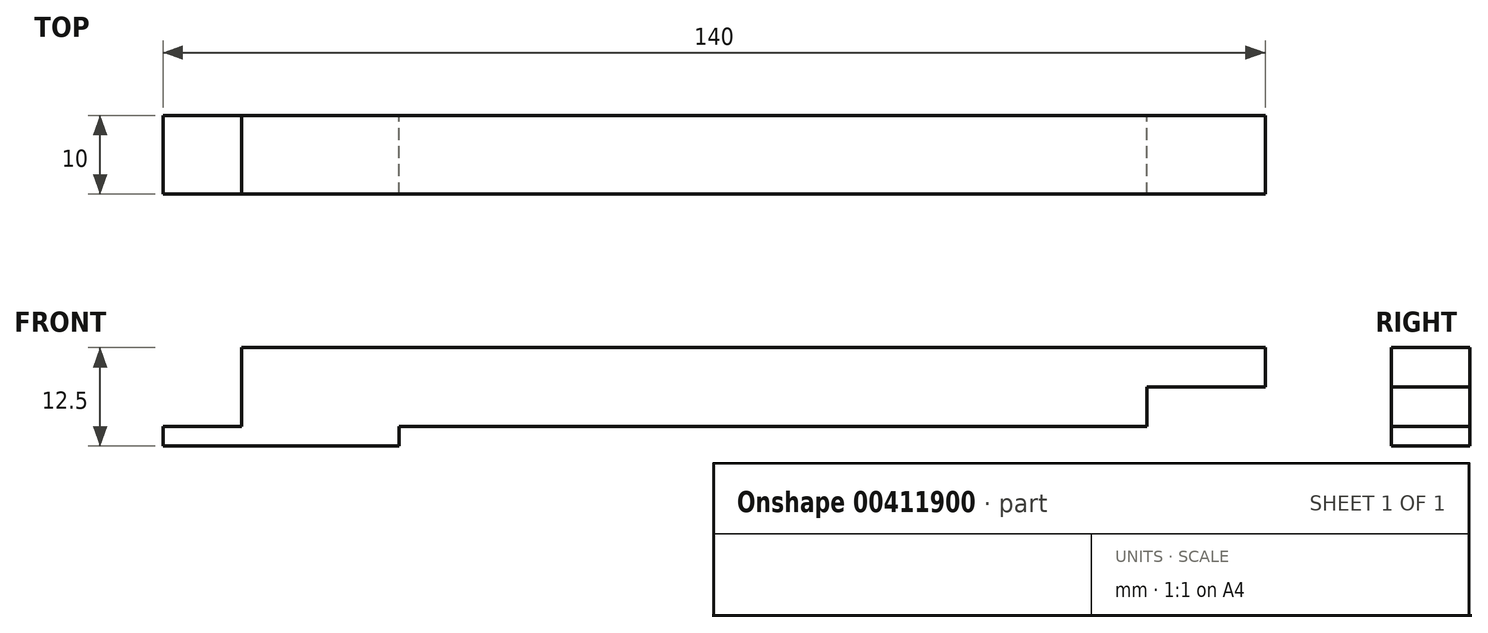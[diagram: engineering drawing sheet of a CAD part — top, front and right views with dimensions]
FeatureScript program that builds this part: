
annotation { "Feature Type Name" : "Feature", "Feature Type Description" : "" }
export const myFeature = defineFeature(function(context is Context, id is Id, definition is map)
    precondition{}
    {
        {
            var Q0;
            Q0=qCreatedBy(makeId("Front.planeOp"),FACE);
            var sketch = newSketch(context, id + "F0", { "sketchPlane" : qUnion([Q0])});
            skLineSegment(sketch, "E0.bottom", {"start": v(-57.5, 0) * mm, "end": v(57.5, 0) * mm});
            skLineSegment(sketch, "E0.top", {"start": v(-57.5, -10) * mm, "end": v(57.5, -10) * mm});
            skLineSegment(sketch, "E0.left", {"start": v(-57.5, 0) * mm, "end": v(-57.5, -10) * mm});
            skLineSegment(sketch, "E0.right", {"start": v(57.5, 0) * mm, "end": v(57.5, -10) * mm});
            skSolve(sketch);
        }
        {
            var Q0;
            Q0 = qSketchRegion(id + "F0", true);
            extrude(context, id + "F1", {"entities" : qUnion([Q0]), "depth" : 10 * mm});
        }
        {
            var Q0;
            Q0=makeQuery(id+"F1.opExtrude","SWEPT_FACE",FACE,{"disambiguationData":[OSD([sQuery(id+"F0.wireOp",EDGE,"E0.top")])]});
            var sketch = newSketch(context, id + "F2", { "sketchPlane" : qUnion([Q0])});
            skLineSegment(sketch, "E1.bottom", {"start": v(57.5, 10) * mm, "end": v(42.5, 10) * mm});
            skLineSegment(sketch, "E1.top", {"start": v(57.5, 0) * mm, "end": v(42.5, 0) * mm});
            skLineSegment(sketch, "E1.left", {"start": v(57.5, 10) * mm, "end": v(57.5, 0) * mm});
            skLineSegment(sketch, "E1.right", {"start": v(42.5, 10) * mm, "end": v(42.5, 0) * mm});
            skSolve(sketch);
        }
        {
            var Q0;
            Q0=makeQuery(id+"F2.imprint","IMPRINT",FACE,{"disambiguationData":[TD([[makeQuery(id+"F2.imprint","IMPRINT",EDGE,{"derivedFrom":sQuery(id+"F2.wireOp",EDGE,"E1.bottom")}),-1.0]])]});
            extrude(context, id + "F3", {"entities" : qUnion([Q0]), "operationType" : NewBodyOperationType.REMOVE, "oppositeDirection" : true, "depth" : 5 * mm});
        }
        {
            var Q0;
            Q0=makeQuery(id+"F1.opExtrude","SWEPT_FACE",FACE,{"disambiguationData":[OSD([sQuery(id+"F0.wireOp",EDGE,"E0.top")])]});
            var sketch = newSketch(context, id + "F4", { "sketchPlane" : qUnion([Q0])});
            skLineSegment(sketch, "E2.bottom", {"start": v(-52.5, 10) * mm, "end": v(-77.5, 10) * mm});
            skLineSegment(sketch, "E2.top", {"start": v(-52.5, 0) * mm, "end": v(-77.5, 0) * mm});
            skLineSegment(sketch, "E2.left", {"start": v(-52.5, 10) * mm, "end": v(-52.5, 0) * mm});
            skLineSegment(sketch, "E2.right", {"start": v(-77.5, 10) * mm, "end": v(-77.5, 0) * mm});
            skSolve(sketch);
        }
        {
            var Q0;
            {var subQ3=sQuery(id+"F4.wireOp",EDGE,"E2.left");Q0=makeQuery(id+"F4.imprint","IMPRINT",FACE,{"disambiguationData":[TD([[makeQuery(id+"F4.imprint","IMPRINT",EDGE,{"derivedFrom":subQ3}),-1.0]])]});}
            var Q1;
            {var subQ2=sQuery(id+"F4.wireOp",EDGE,"E2.right");Q1=makeQuery(id+"F4.imprint","IMPRINT",FACE,{"disambiguationData":[TD([[makeQuery(id+"F4.imprint","IMPRINT",EDGE,{"derivedFrom":subQ2}),1.0]])]});}
            extrude(context, id + "F5", {"entities" : qUnion([Q0, Q1]), "operationType" : NewBodyOperationType.ADD, "depth" : 2.5 * mm});
        }
        {
            var Q0;
            Q0=makeQuery(id+"F1.opExtrude","SWEPT_FACE",FACE,{"disambiguationData":[OSD([sQuery(id+"F0.wireOp",EDGE,"E0.left")])]});
            extrude(context, id + "F6", {"entities" : qUnion([Q0]), "operationType" : NewBodyOperationType.ADD, "depth" : 15 * mm});
        }
        {
            var Q0;
            Q0=makeQuery(id+"F5.opExtrude","SWEPT_FACE",FACE,{"disambiguationData":[OSD([sQuery(id+"F4.wireOp",EDGE,"E2.right")])]});
            extrude(context, id + "F7", {"entities" : qUnion([Q0]), "operationType" : NewBodyOperationType.ADD, "depth" : 5 * mm});
        }
    });
